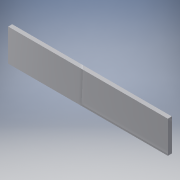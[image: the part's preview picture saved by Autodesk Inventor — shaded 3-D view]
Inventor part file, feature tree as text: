
AUTODESK INVENTOR PART (.ipt)
format: ipt  version: 2016 (Build 200138000, 138)  size: 102,912 bytes
history: native  units: in
note: dims shown in document units (in); Inventor stores cm internally (conversion verified against a paired STEP export)
features: extrude x2, sketch x2
ambient origin geometry x8: Origin, YZ Plane, XZ Plane, XY Plane, X Axis, Y Axis, Z Axis, Center Point
bodies: Solid1 (feature_tree)
feature tree (4):
  extrude  "Extrusion1"  Depth=1.0in
  extrude  "Extrusion2"  Depth=0.125in
  sketch  "Sketch1"  dims[d0=4.975in d1=1.0in]
  sketch  "Sketch2"  dims[d2=0.125in d3=0.0in d4=0.2656in d5=0.5in d6=0.5in d7=1.0in d8=0.5in d9=0.125in d10=0.0in]
